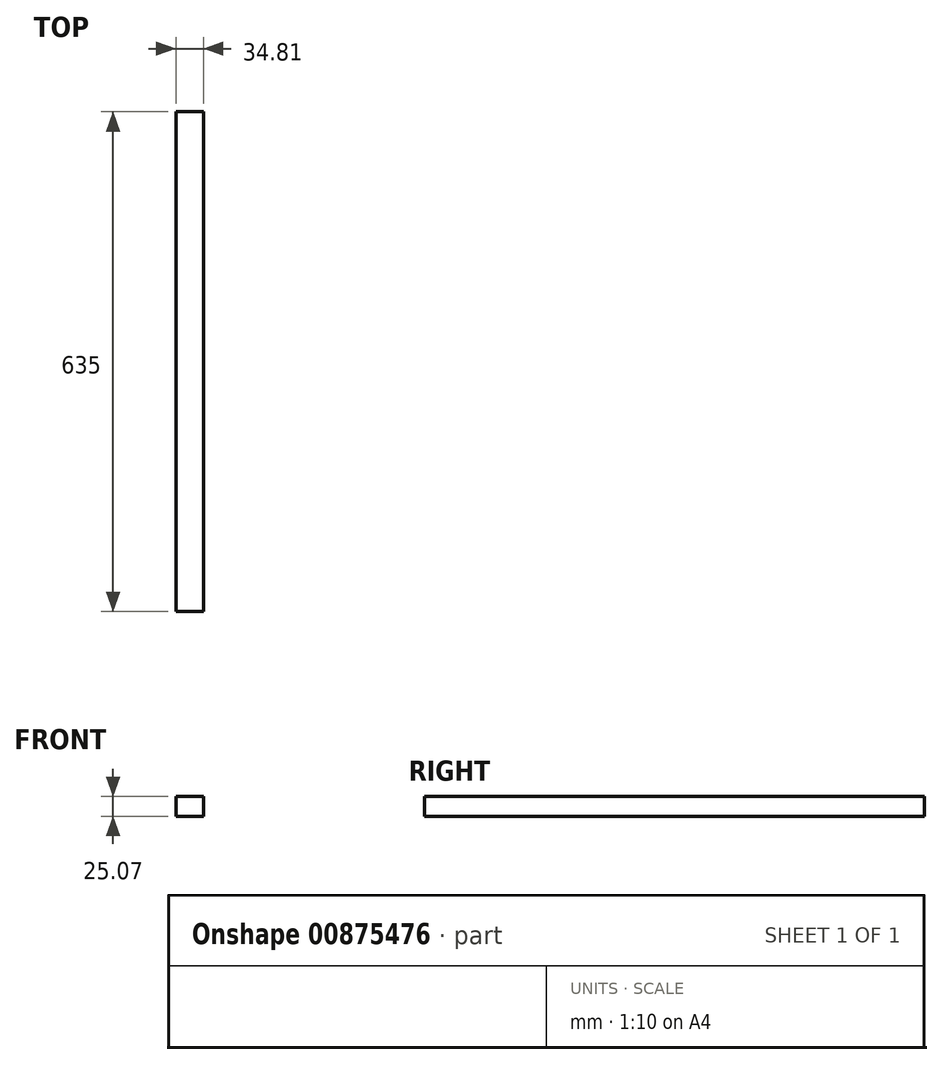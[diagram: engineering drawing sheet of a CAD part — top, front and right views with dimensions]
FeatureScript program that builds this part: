
annotation { "Feature Type Name" : "Feature", "Feature Type Description" : "" }
export const myFeature = defineFeature(function(context is Context, id is Id, definition is map)
    precondition{}
    {
        {
            var Q0;
            Q0=qCreatedBy(makeId("Front.planeOp"),FACE);
            var sketch = newSketch(context, id + "F0", { "sketchPlane" : qUnion([Q0])});
            skLineSegment(sketch, "E0", {"start": v(32.6, 47.17) * mm, "end": v(30.44, 45.38) * mm});
            skPoint(sketch, "E1.oppositeSnap0", {"position": v(16.3, 33.66) * mm});
            skLineSegment(sketch, "E1.bottom", {"start": v(44.9, 45.38) * mm, "end": v(30.44, 45.38) * mm});
            skLineSegment(sketch, "E1.top", {"start": v(44.9, 20.16) * mm, "end": v(16.3, 20.16) * mm});
            skLineSegment(sketch, "E1.left", {"start": v(44.9, 45.38) * mm, "end": v(44.9, 20.16) * mm});
            skLineSegment(sketch, "E1.right", {"start": v(16.3, 45.38) * mm, "end": v(16.3, 20.16) * mm});
            skLineSegment(sketch, "E2.bottom", {"start": v(0, 20.16) * mm, "end": v(0, 20.16) * mm});
            skLineSegment(sketch, "E2.top", {"start": v(0, 0) * mm, "end": v(0, 0) * mm});
            skLineSegment(sketch, "E2.left", {"start": v(0, 20.16) * mm, "end": v(0, 0) * mm});
            skLineSegment(sketch, "E3.bottom", {"start": v(14.84, -16.42) * mm, "end": v(49.65, -16.42) * mm});
            skLineSegment(sketch, "E3.top", {"start": v(14.84, -41.5) * mm, "end": v(49.65, -41.5) * mm});
            skLineSegment(sketch, "E3.left", {"start": v(14.84, -16.42) * mm, "end": v(14.84, -41.5) * mm});
            skLineSegment(sketch, "E3.right", {"start": v(49.65, -16.42) * mm, "end": v(49.65, -41.5) * mm});
            skSolve(sketch);
        }
        {
            var Q0;
            Q0=makeQuery(id+"F0.imprint","IMPRINT",FACE,{"disambiguationData":[TD([[makeQuery(id+"F0.imprint","IMPRINT",EDGE,{"derivedFrom":sQuery(id+"F0.wireOp",EDGE,"E3.bottom")}),-1.0]])]});
            extrude(context, id + "F1", {"entities" : qUnion([Q0]), "depth" : 635 * mm, "offsetDistance" : 25.4 * mm});
        }
    });
